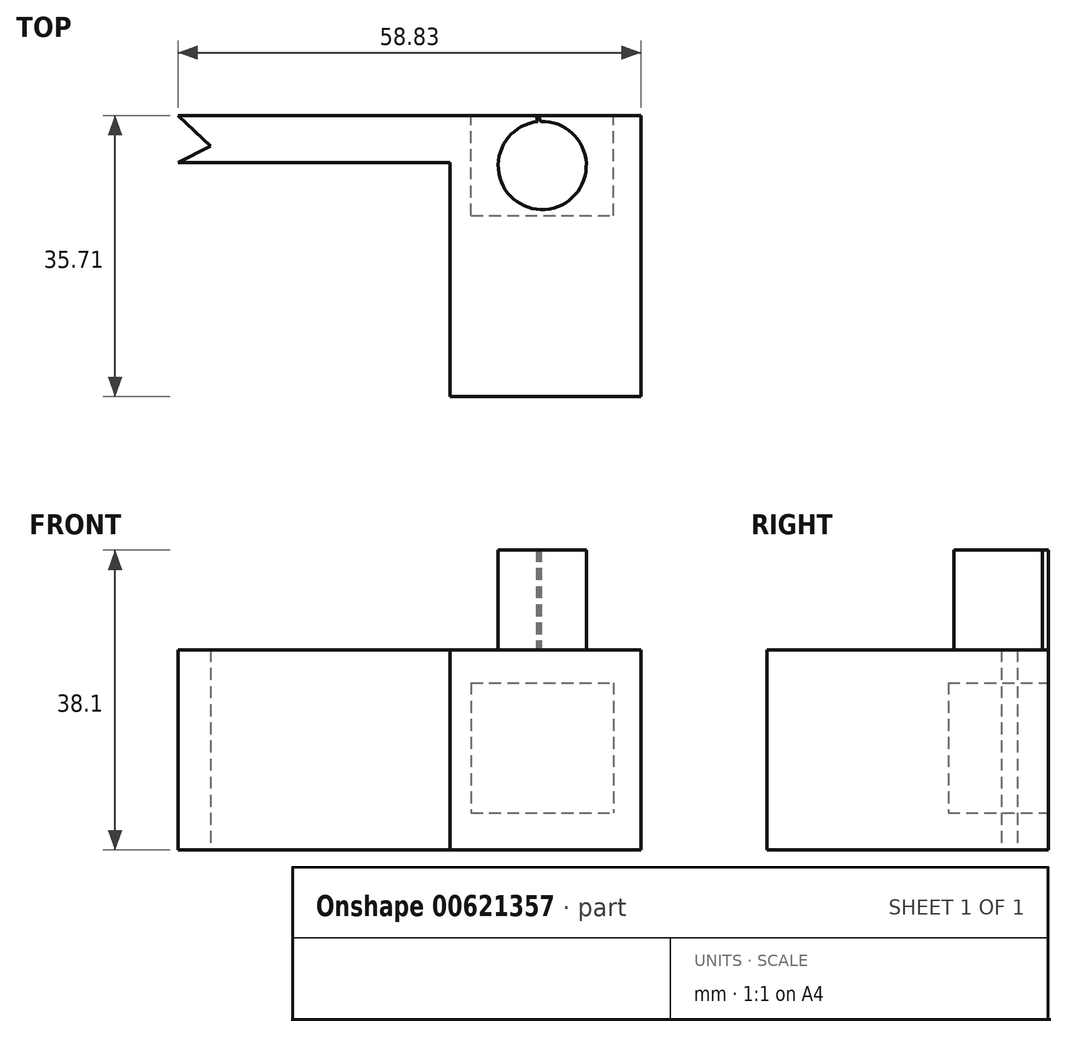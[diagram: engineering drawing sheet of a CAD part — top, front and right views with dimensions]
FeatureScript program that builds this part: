
annotation { "Feature Type Name" : "Feature", "Feature Type Description" : "" }
export const myFeature = defineFeature(function(context is Context, id is Id, definition is map)
    precondition{}
    {
        {
            var Q0;
            Q0=qCreatedBy(makeId("Top.planeOp"),FACE);
            var sketch = newSketch(context, id + "F0", { "sketchPlane" : qUnion([Q0])});
            skLineSegment(sketch, "E0", {"start": v(0, 0) * mm, "end": v(0, 35.71) * mm});
            skLineSegment(sketch, "E1", {"start": v(0, 35.71) * mm, "end": v(-58.83, 35.71) * mm});
            skLineSegment(sketch, "E2", {"start": v(-58.83, 35.71) * mm, "end": v(-54.71, 31.82) * mm});
            skLineSegment(sketch, "E3", {"start": v(-54.71, 31.82) * mm, "end": v(-58.83, 29.76) * mm});
            skLineSegment(sketch, "E4", {"start": v(-58.83, 29.76) * mm, "end": v(-24.27, 29.76) * mm});
            skLineSegment(sketch, "E5", {"start": v(-24.27, 29.76) * mm, "end": v(-24.27, 21.3) * mm});
            skLineSegment(sketch, "E6", {"start": v(-24.27, 21.3) * mm, "end": v(0, 21.3) * mm});
            skLineSegment(sketch, "E7", {"start": v(-24.27, 21.3) * mm, "end": v(-24.27, 0) * mm});
            skLineSegment(sketch, "E8", {"start": v(-24.27, 0) * mm, "end": v(0, 0) * mm});
            skLineSegment(sketch, "E9", {"start": v(0, 0) * mm, "end": v(-24.27, 0) * mm});
            skLineSegment(sketch, "E10", {"start": v(0, 34.8) * mm, "end": v(0, 0) * mm});
            skSolve(sketch);
        }
        {
            var Q0;
            {var subQ0=sQuery(id+"F0.wireOp",EDGE,"E6");Q0=makeQuery(id+"F0.imprint","IMPRINT",FACE,{"disambiguationData":[TD([[makeQuery(id+"F0.imprint","IMPRINT",EDGE,{"derivedFrom":subQ0}),-1.0]])]});}
            var Q1;
            Q1=makeQuery(id+"F0.imprint","IMPRINT",FACE,{"disambiguationData":[TD([[makeQuery(id+"F0.imprint","IMPRINT",EDGE,{"derivedFrom":sQuery(id+"F0.wireOp",EDGE,"E1")}),1.0]])]});
            extrude(context, id + "F1", {"entities" : qUnion([Q0, Q1]), "depth" : 25.4 * mm, "offsetDistance" : 25.4 * mm});
        }
        {
            var Q0;
            Q0=makeQuery(id+"F1.opExtrude","SWEPT_FACE",FACE,{"disambiguationData":[OSD([sQuery(id+"F0.wireOp",EDGE,"E1")])]});
            var sketch = newSketch(context, id + "F2", { "sketchPlane" : qUnion([Q0])});
            skLineSegment(sketch, "E11", {"start": v(21.6, 25.4) * mm, "end": v(21.6, 0) * mm});
            skLineSegment(sketch, "E12", {"start": v(21.6, 4.69) * mm, "end": v(0, 4.69) * mm});
            skLineSegment(sketch, "E13", {"start": v(21.6, 21.24) * mm, "end": v(0, 21.24) * mm});
            skPoint(sketch, "E13.endSnap0", {"position": v(0, 12.7) * mm});
            skLineSegment(sketch, "E14", {"start": v(3.52, 21.24) * mm, "end": v(3.52, 4.69) * mm});
            skSolve(sketch);
        }
        {
            var Q0;
            {var subQ5=sQuery(id+"F2.wireOp",EDGE,"E14");Q0=makeQuery(id+"F2.imprint","IMPRINT",FACE,{"disambiguationData":[TD([[makeQuery(id+"F2.imprint","IMPRINT",EDGE,{"derivedFrom":subQ5}),1.0]])]});}
            extrude(context, id + "F3", {"entities" : qUnion([Q0]), "operationType" : NewBodyOperationType.REMOVE, "oppositeDirection" : true, "depth" : 12.7 * mm, "offsetDistance" : 25.4 * mm});
        }
        {
            var Q0;
            Q0=makeQuery(id+"F1.opExtrude","CAP_FACE",FACE,{"disambiguationData":[OSD([sQuery(id+"F0.wireOp",EDGE,"E1"),sQuery(id+"F0.wireOp",EDGE,"E2"),sQuery(id+"F0.wireOp",EDGE,"E3"),sQuery(id+"F0.wireOp",EDGE,"E4"),sQuery(id+"F0.wireOp",EDGE,"E5"),sQuery(id+"F0.wireOp",EDGE,"E7"),sQuery(id+"F0.wireOp",EDGE,"E9"),sQuery(id+"F0.wireOp",EDGE,"E0"),sQuery(id+"F0.wireOp",EDGE,"E10")])],"isStart":false});
            var sketch = newSketch(context, id + "F4", { "sketchPlane" : qUnion([Q0])});
            skLineSegment(sketch, "E15.0", {"start": v(-21.6, 35.71) * mm, "end": v(-3.52, 35.71) * mm});
            skLineSegment(sketch, "E16.0.0", {"start": v(-3.52, 35.71) * mm, "end": v(-21.6, 35.71) * mm});
            skLineSegment(sketch, "E16.0.1", {"start": v(-21.6, 35.71) * mm, "end": v(-21.6, 23.01) * mm});
            skLineSegment(sketch, "E16.0.2", {"start": v(-21.6, 23.01) * mm, "end": v(-3.52, 23.01) * mm});
            skLineSegment(sketch, "E16.0.3", {"start": v(-3.52, 23.01) * mm, "end": v(-3.52, 35.71) * mm});
            skArc(sketch, "E17", {"start": v(-13.13, 34.93) * mm, "mid": v(-12.19, 23.78) * mm, "end": v(-12.74, 34.96) * mm});
            skPoint(sketch, "E17.centerSnap0", {"position": v(-3.52, 29.36) * mm});
            skPoint(sketch, "E17.centerSnap1", {"position": v(-12.56, 35.71) * mm});
            skArc(sketch, "E18", {"start": v(-12.87, 36.05) * mm, "mid": v(-12.91, 35.5) * mm, "end": v(-12.74, 34.96) * mm});
            skArc(sketch, "E19.0", {"start": v(-13.23, 36.05) * mm, "mid": v(-13.27, 35.48) * mm, "end": v(-13.13, 34.93) * mm});
            skLineSegment(sketch, "E20", {"start": v(-12.87, 36.05) * mm, "end": v(-13.23, 36.05) * mm});
            skSolve(sketch);
        }
        {
            var Q0;
            Q0=makeQuery(id+"F4.imprint","IMPRINT",FACE,{"disambiguationData":[TD([[makeQuery(id+"F4.imprint","IMPRINT",EDGE,{"derivedFrom":sQuery(id+"F4.wireOp",EDGE,"E17")}),1.0]])]});
            extrude(context, id + "F5", {"entities" : qUnion([Q0]), "operationType" : NewBodyOperationType.ADD, "depth" : 12.7 * mm, "offsetDistance" : 25.4 * mm});
        }
    });
